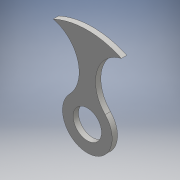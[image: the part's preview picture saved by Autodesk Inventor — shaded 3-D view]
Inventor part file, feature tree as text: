
AUTODESK INVENTOR PART (.ipt)
format: ipt  version: 2016 (Build 200138000, 138)  size: 110,080 bytes
history: native  units: mm
features: extrude x1, sketch x1
ambient origin geometry x8: Origin, YZ Plane, XZ Plane, XY Plane, X Axis, Y Axis, Z Axis, Center Point
bodies: Body1 (feature_tree)
feature tree (2):
  extrude  "Extrusion3"  Depth=9.6mm
  sketch  "Sketch1"  dims[d0=8.0mm d1=14.0mm d2=46.0mm d11=1.5mm d12=0.0mm d15=9.6mm d17=4.6mm]
